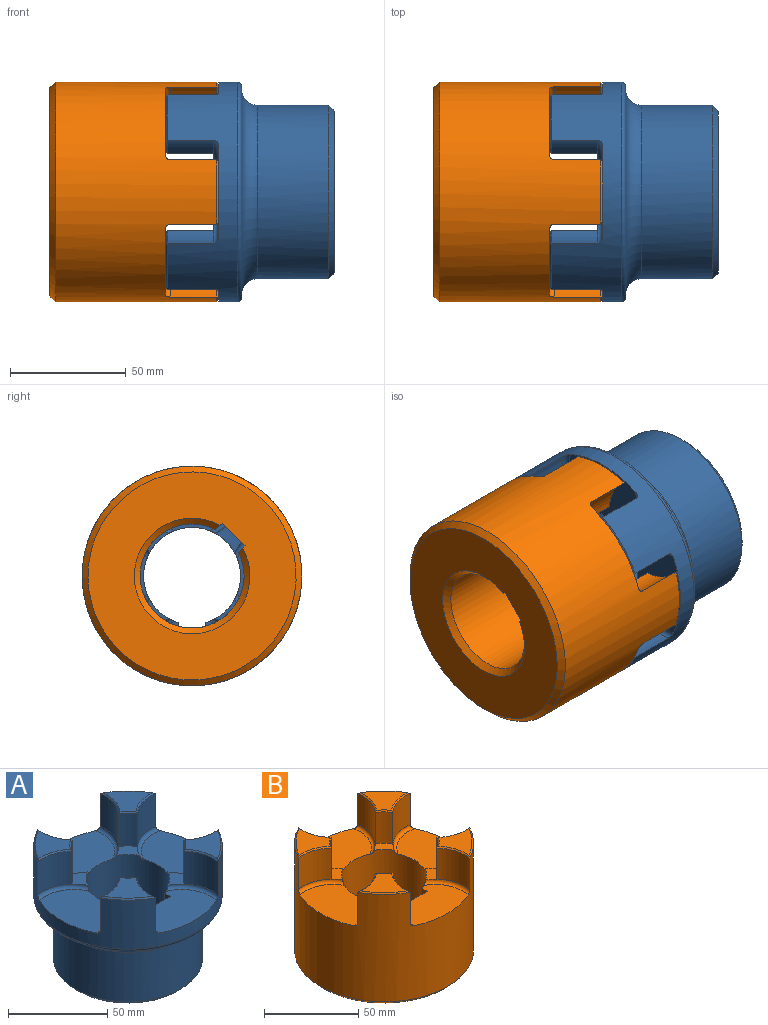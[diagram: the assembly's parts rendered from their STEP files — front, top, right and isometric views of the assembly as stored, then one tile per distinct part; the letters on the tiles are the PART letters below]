
ASSEMBLY  parts=2 mates=1
PART A: 60 faces, bbox 107.1x107.1x73 mm
  f0: cylinder r=21mm len=49.5mm, axis (0,0,1), area 5793mm2, adj f1,f5,f6,f7,f12,f16,f20,f29
  f1: cone r=21mm half-angle=45deg, axis (0,0,-1), area 451.2mm2, adj f0,f25,f33,f34
  f2: cylinder r=22.5mm len=20.25mm, axis (0,0,1), area 410.7mm2, adj f21,f28,f42,f52
  f3: cylinder r=22.5mm len=20.25mm, axis (0,0,1), area 410.7mm2, adj f9,f21,f46,f53
  f4: cylinder r=22.5mm len=20.25mm, axis (0,0,1), area 410.7mm2, adj f13,f21,f50,f54
  f5: plane 13.11x13.11mm, normal (0,0,1), area 76.3mm2, adj f0,f9,f53,f56
  f6: plane 13.11x13.11mm, normal (0,0,1), area 76.3mm2, adj f0,f13,f54,f57
  f7: plane 13.11x13.11mm, normal (0,0,1), area 76.3mm2, adj f0,f17,f55,f58
  f8: cylinder r=22.5mm len=20.25mm, axis (0,0,1), area 410.7mm2, adj f17,f21,f38,f55
  f9: cylinder r=28.5mm len=20.25mm, axis (0,0,1), area 192.9mm2, adj f3,f5,f11,f47
  f10: plane 22.99x22.99mm, normal (0,0,1), area 245.2mm2, adj f44,f45,f46,f47
  f11: cylinder r=22.5mm len=20.25mm, axis (0,0,1), area 410.7mm2, adj f9,f21,f45,f56
  f12: plane 41x27.98mm, normal (0,0,1), area 934.2mm2, adj f0,f21,f52,f56
  f13: cylinder r=28.5mm len=20.25mm, axis (0,0,1), area 192.9mm2, adj f4,f6,f15,f51
  f14: plane 22.99x22.99mm, normal (0,0,1), area 245.2mm2, adj f48,f49,f50,f51
  f15: cylinder r=22.5mm len=20.25mm, axis (0,0,1), area 410.7mm2, adj f13,f21,f49,f57
  f16: plane 41x27.98mm, normal (0,0,1), area 934.2mm2, adj f0,f21,f53,f57
  f17: cylinder r=28.5mm len=20.25mm, axis (0,0,1), area 192.9mm2, adj f7,f8,f19,f39
  f18: plane 22.99x22.99mm, normal (0,0,1), area 245.2mm2, adj f36,f37,f38,f39
  f19: cylinder r=22.5mm len=20.25mm, axis (0,0,1), area 410.7mm2, adj f17,f21,f37,f58
  f20: plane 41x27.98mm, normal (0,0,1), area 934.2mm2, adj f0,f21,f54,f58
  f21: cylinder r=47.5mm len=95mm, axis (0,0,-1), area 4919mm2, adj f2,f3,f4,f8,f11,f12,f15,f16
  f22: plane 22.99x22.99mm, normal (0,0,1), area 245.2mm2, adj f40,f41,f42,f43
  f23: cylinder r=37.5mm len=75mm, axis (0,0,-1), area 7186.4mm2, adj f26,f32
  f24: plane 91x91mm, normal (0,0,-1), area 282.7mm2, adj f26,f27
  f25: plane 70x70mm, normal (0,0,-1), area 2102.9mm2, adj f1,f32,f33,f34,f35
  f26: torus R=44.5mm, axis (0,0,-1), area 2766.5mm2, adj f23,f24
  f27: torus R=45.5mm, axis (0,0,-1), area 923.3mm2, adj f21,f24
  f28: cylinder r=28.5mm len=20.25mm, axis (0,0,1), area 192.9mm2, adj f2,f29,f31,f43
  f29: plane 13.11x13.11mm, normal (0,0,1), area 76.3mm2, adj f0,f28,f52,f59
  f30: plane 41x27.98mm, normal (0,0,1), area 893.2mm2, adj f0,f21,f33,f34,f35,f55,f59
  f31: cylinder r=22.5mm len=20.25mm, axis (0,0,1), area 410.7mm2, adj f21,f28,f41,f59
  f32: cone r=35mm half-angle=45deg, axis (0,0,1), area 805.3mm2, adj f23,f25
  f33: plane 50.04x4.04mm, normal (1,0,0), area 196.7mm2, adj f0,f1,f25,f30,f35
  f34: plane 50.04x4.04mm, normal (-1,0,0), area 196.7mm2, adj f0,f1,f25,f30,f35
  f35: plane 50x12mm, normal (0,1,0), area 600mm2, adj f25,f30,f33,f34
  f36: cone r=46.75mm half-angle=45deg, axis (0,0,-1), area 28.3mm2, adj f18,f21,f37,f38
  f37: cone r=22.5mm half-angle=45deg, axis (0,0,1), area 20.6mm2, adj f18,f19,f36,f39
  f38: cone r=22.5mm half-angle=45deg, axis (0,0,1), area 20.6mm2, adj f8,f18,f36,f39
  f39: cone r=28.5mm half-angle=45deg, axis (0,0,1), area 9.4mm2, adj f17,f18,f37,f38
  f40: cone r=46.75mm half-angle=45deg, axis (0,0,-1), area 28.3mm2, adj f21,f22,f41,f42
  f41: cone r=22.5mm half-angle=45deg, axis (0,0,1), area 20.6mm2, adj f22,f31,f40,f43
  f42: cone r=22.5mm half-angle=45deg, axis (0,0,1), area 20.6mm2, adj f2,f22,f40,f43
  f43: cone r=28.5mm half-angle=45deg, axis (0,0,1), area 9.4mm2, adj f22,f28,f41,f42
  f44: cone r=46.75mm half-angle=45deg, axis (0,0,-1), area 28.3mm2, adj f10,f21,f45,f46
  f45: cone r=22.5mm half-angle=45deg, axis (0,0,1), area 20.6mm2, adj f10,f11,f44,f47
  f46: cone r=22.5mm half-angle=45deg, axis (0,0,1), area 20.6mm2, adj f3,f10,f44,f47
  f47: cone r=28.5mm half-angle=45deg, axis (0,0,1), area 9.4mm2, adj f9,f10,f45,f46
  f48: cone r=46.75mm half-angle=45deg, axis (0,0,-1), area 28.3mm2, adj f14,f21,f49,f50
  f49: cone r=22.5mm half-angle=45deg, axis (0,0,1), area 20.6mm2, adj f14,f15,f48,f51
  f50: cone r=22.5mm half-angle=45deg, axis (0,0,1), area 20.6mm2, adj f4,f14,f48,f51
  f51: cone r=28.5mm half-angle=45deg, axis (0,0,1), area 9.4mm2, adj f13,f14,f49,f50
  f52: torus R=20.5mm, axis (0,0,1), area 89.6mm2, adj f0,f2,f12,f21,f29
  f53: torus R=20.5mm, axis (0,0,1), area 89.6mm2, adj f0,f3,f5,f16,f21
  f54: torus R=20.5mm, axis (0,0,1), area 89.6mm2, adj f0,f4,f6,f20,f21
  f55: torus R=20.5mm, axis (0,0,1), area 89.6mm2, adj f0,f7,f8,f21,f30
  f56: torus R=20.5mm, axis (0,0,1), area 89.6mm2, adj f0,f5,f11,f12,f21
  f57: torus R=20.5mm, axis (0,0,1), area 89.6mm2, adj f0,f6,f15,f16,f21
  f58: torus R=20.5mm, axis (0,0,1), area 89.6mm2, adj f0,f7,f19,f20,f21
  f59: torus R=20.5mm, axis (0,0,1), area 89.6mm2, adj f0,f21,f29,f30,f31
PART B: 56 faces, bbox 95x95x73 mm
  f0: cylinder r=22.5mm len=49.5mm, axis (0,0,-1), area 6133.7mm2, adj f1,f2,f3,f4,f5,f6,f7,f26
  f1: plane 11.58x11.58mm, normal (0,0,1), area 59.2mm2, adj f0,f12,f45,f48
  f2: plane 11.58x11.58mm, normal (0,0,1), area 59.2mm2, adj f0,f15,f46,f49
  f3: plane 11.58x11.58mm, normal (0,0,1), area 59.2mm2, adj f0,f18,f47,f50
  f4: plane 11.58x11.58mm, normal (0,0,1), area 59.2mm2, adj f0,f25,f44,f51
  f5: plane 41x27.13mm, normal (0,0,1), area 907.4mm2, adj f0,f21,f45,f49
  f6: plane 41x27.13mm, normal (0,0,1), area 907.4mm2, adj f0,f21,f46,f50
  f7: plane 41x27.13mm, normal (0,0,1), area 861.9mm2, adj f0,f21,f47,f51,f52,f53,f54
  f8: cylinder r=22.5mm len=20.25mm, axis (0,0,1), area 410.7mm2, adj f21,f25,f34,f44
  f9: cylinder r=22.5mm len=20.25mm, axis (0,0,1), area 410.7mm2, adj f12,f21,f38,f45
  f10: cylinder r=22.5mm len=20.25mm, axis (0,0,1), area 410.7mm2, adj f15,f21,f42,f46
  f11: cylinder r=22.5mm len=20.25mm, axis (0,0,1), area 410.7mm2, adj f18,f21,f30,f47
  f12: cylinder r=28.5mm len=20.25mm, axis (0,0,1), area 192.9mm2, adj f1,f9,f14,f39
  f13: plane 22.99x22.99mm, normal (0,0,1), area 245.2mm2, adj f36,f37,f38,f39
  f14: cylinder r=22.5mm len=20.25mm, axis (0,0,1), area 410.7mm2, adj f12,f21,f37,f48
  f15: cylinder r=28.5mm len=20.25mm, axis (0,0,1), area 192.9mm2, adj f2,f10,f17,f43
  f16: plane 22.99x22.99mm, normal (0,0,1), area 245.2mm2, adj f40,f41,f42,f43
  f17: cylinder r=22.5mm len=20.25mm, axis (0,0,1), area 410.7mm2, adj f15,f21,f41,f49
  f18: cylinder r=28.5mm len=20.25mm, axis (0,0,1), area 192.9mm2, adj f3,f11,f20,f31
  f19: plane 22.99x22.99mm, normal (0,0,1), area 245.2mm2, adj f28,f29,f30,f31
  f20: cylinder r=22.5mm len=20.25mm, axis (0,0,1), area 410.7mm2, adj f18,f21,f29,f50
  f21: cylinder r=47.5mm len=95mm, axis (0,0,-1), area 16707.8mm2, adj f5,f6,f7,f8,f9,f10,f11,f14
  f22: plane 22.99x22.99mm, normal (0,0,1), area 245.2mm2, adj f32,f33,f34,f35
  f23: plane 90x90mm, normal (0,0,-1), area 4388.2mm2, adj f24,f52,f53,f54,f55
  f24: cone r=47.5mm half-angle=45deg, axis (0,0,1), area 1027.4mm2, adj f21,f23
  f25: cylinder r=28.5mm len=20.25mm, axis (0,0,1), area 192.9mm2, adj f4,f8,f27,f35
  f26: plane 41x27.13mm, normal (0,0,1), area 907.4mm2, adj f0,f21,f44,f48
  f27: cylinder r=22.5mm len=20.25mm, axis (0,0,1), area 410.7mm2, adj f21,f25,f33,f51
  f28: cone r=46.75mm half-angle=45deg, axis (0,0,-1), area 28.3mm2, adj f19,f21,f29,f30
  f29: cone r=22.5mm half-angle=45deg, axis (0,0,1), area 20.6mm2, adj f19,f20,f28,f31
  f30: cone r=22.5mm half-angle=45deg, axis (0,0,1), area 20.6mm2, adj f11,f19,f28,f31
  f31: cone r=28.5mm half-angle=45deg, axis (0,0,1), area 9.4mm2, adj f18,f19,f29,f30
  f32: cone r=46.75mm half-angle=45deg, axis (0,0,-1), area 28.3mm2, adj f21,f22,f33,f34
  f33: cone r=22.5mm half-angle=45deg, axis (0,0,1), area 20.6mm2, adj f22,f27,f32,f35
  f34: cone r=22.5mm half-angle=45deg, axis (0,0,1), area 20.6mm2, adj f8,f22,f32,f35
  f35: cone r=28.5mm half-angle=45deg, axis (0,0,1), area 9.4mm2, adj f22,f25,f33,f34
  f36: cone r=46.75mm half-angle=45deg, axis (0,0,-1), area 28.3mm2, adj f13,f21,f37,f38
  f37: cone r=22.5mm half-angle=45deg, axis (0,0,1), area 20.6mm2, adj f13,f14,f36,f39
  f38: cone r=22.5mm half-angle=45deg, axis (0,0,1), area 20.6mm2, adj f9,f13,f36,f39
  f39: cone r=28.5mm half-angle=45deg, axis (0,0,1), area 9.4mm2, adj f12,f13,f37,f38
  f40: cone r=46.75mm half-angle=45deg, axis (0,0,-1), area 28.3mm2, adj f16,f21,f41,f42
  f41: cone r=22.5mm half-angle=45deg, axis (0,0,1), area 20.6mm2, adj f16,f17,f40,f43
  f42: cone r=22.5mm half-angle=45deg, axis (0,0,1), area 20.6mm2, adj f10,f16,f40,f43
  f43: cone r=28.5mm half-angle=45deg, axis (0,0,1), area 9.4mm2, adj f15,f16,f41,f42
  f44: torus R=20.5mm, axis (0,0,1), area 83.8mm2, adj f0,f4,f8,f21,f26
  f45: torus R=20.5mm, axis (0,0,1), area 83.8mm2, adj f0,f1,f5,f9,f21
  f46: torus R=20.5mm, axis (0,0,1), area 83.8mm2, adj f0,f2,f6,f10,f21
  f47: torus R=20.5mm, axis (0,0,1), area 83.8mm2, adj f0,f3,f7,f11,f21
  f48: torus R=20.5mm, axis (0,0,1), area 83.8mm2, adj f0,f1,f14,f21,f26
  f49: torus R=20.5mm, axis (0,0,1), area 83.8mm2, adj f0,f2,f5,f17,f21
  f50: torus R=20.5mm, axis (0,0,1), area 83.8mm2, adj f0,f3,f6,f20,f21
  f51: torus R=20.5mm, axis (0,0,1), area 83.8mm2, adj f0,f4,f7,f21,f27
  f52: plane 50.04x4.04mm, normal (1,0,0), area 196.7mm2, adj f0,f7,f23,f54,f55
  f53: plane 50.04x4.04mm, normal (-1,0,0), area 196.7mm2, adj f0,f7,f23,f54,f55
  f54: plane 50x14mm, normal (0,1,0), area 700mm2, adj f7,f23,f52,f53
  f55: cone r=22.5mm half-angle=45deg, axis (0,0,-1), area 477.2mm2, adj f0,f23,f52,f53
PLACE A rot(axis=(0.58,-0.58,-0.58),120deg) t=(34.89,54.38,-4.91)mm
PLACE B rot(axis=(-0.36,0.86,-0.36),98.4deg) t=(-15.11,54.38,-4.91)mm
MATE fastened B.f0 <-> A.f9  axis (1,0,0) through (-1.61,54.38,-4.91)mm
